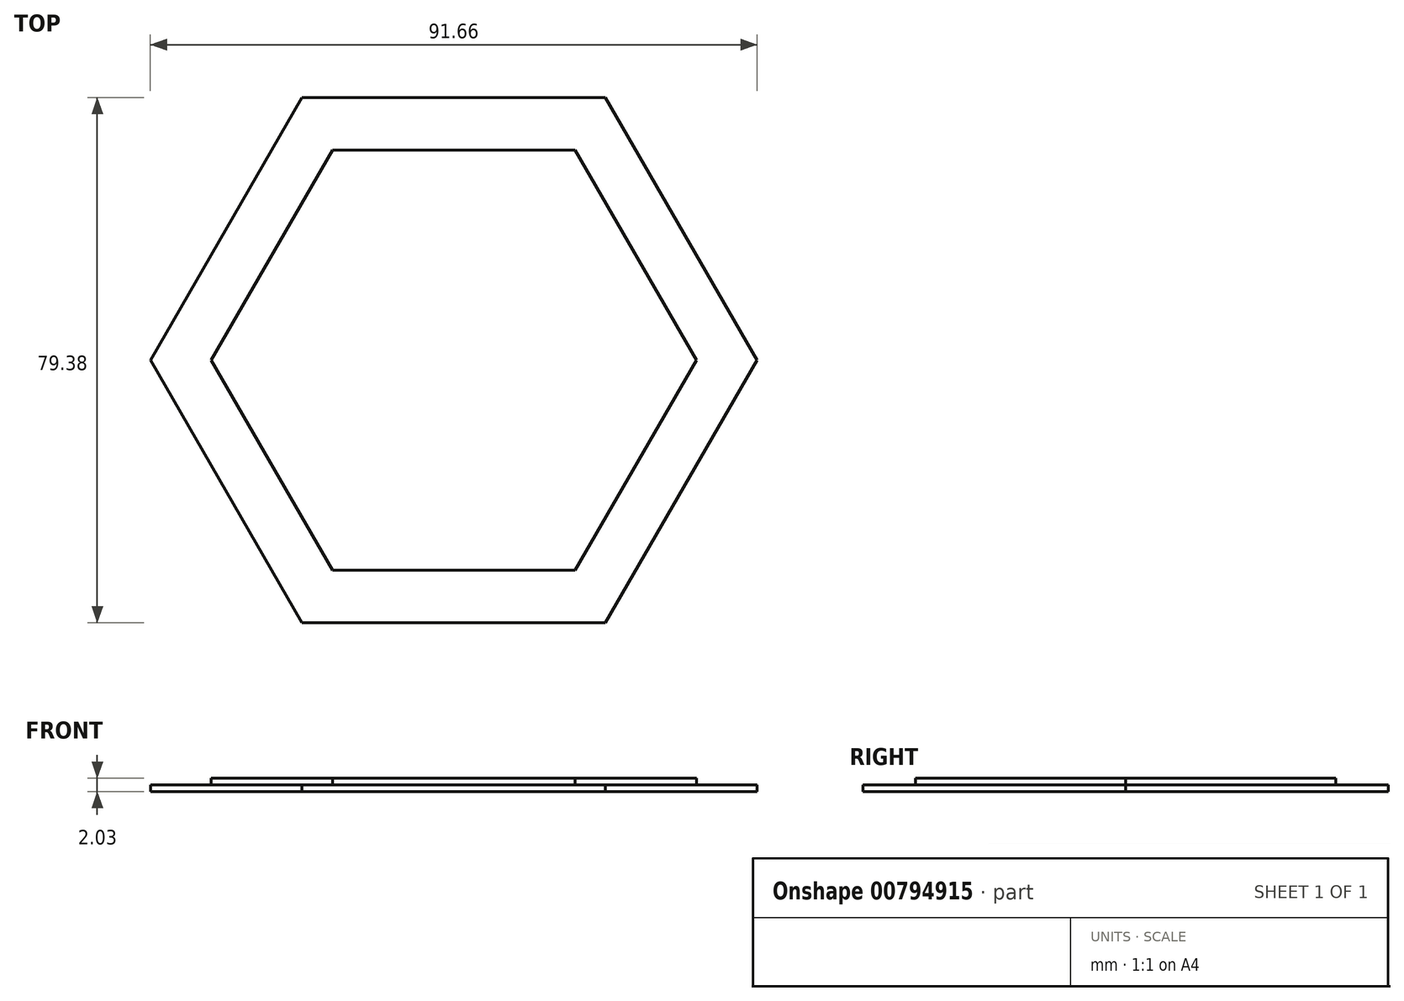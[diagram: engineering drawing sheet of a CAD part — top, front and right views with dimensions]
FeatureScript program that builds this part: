
annotation { "Feature Type Name" : "Feature", "Feature Type Description" : "" }
export const myFeature = defineFeature(function(context is Context, id is Id, definition is map)
    precondition{}
    {
        {
            var Q0;
            Q0=qCreatedBy(makeId("Top.planeOp"),FACE);
            var sketch = newSketch(context, id + "F0", { "sketchPlane" : qUnion([Q0])});
            skCircle(sketch, "E0.cCircle", {"center": v(0, 0) * mm, "radius": 39.69 * mm, "construction": true});
            skLineSegment(sketch, "E0.0", {"start": v(-45.83, 0) * mm, "end": v(-22.91, 39.69) * mm});
            skLineSegment(sketch, "E0.1", {"start": v(-22.91, 39.69) * mm, "end": v(22.91, 39.69) * mm});
            skLineSegment(sketch, "E0.2", {"start": v(22.91, 39.69) * mm, "end": v(45.83, 0) * mm});
            skLineSegment(sketch, "E0.3", {"start": v(45.83, 0) * mm, "end": v(22.91, -39.69) * mm});
            skLineSegment(sketch, "E0.4", {"start": v(22.91, -39.69) * mm, "end": v(-22.91, -39.69) * mm});
            skLineSegment(sketch, "E0.5", {"start": v(-22.91, -39.69) * mm, "end": v(-45.83, 0) * mm});
            skPoint(sketch, "E0.0.midPoint", {"position": v(-34.37, 19.84) * mm});
            skSolve(sketch);
        }
        {
            var Q0;
            Q0=makeQuery(id+"F0.imprint","IMPRINT",FACE,{"disambiguationData":[TD([[makeQuery(id+"F0.imprint","IMPRINT",EDGE,{"derivedFrom":sQuery(id+"F0.wireOp",EDGE,"E0.0")}),-1.0]])]});
            extrude(context, id + "F1", {"entities" : qUnion([Q0]), "depth" : 1.02 * mm, "offsetDistance" : 25.4 * mm});
        }
        {
            var Q0;
            Q0=makeQuery(id+"F1.opExtrude","CAP_FACE",FACE,{"disambiguationData":[OSD([sQuery(id+"F0.wireOp",EDGE,"E0.0"),sQuery(id+"F0.wireOp",EDGE,"E0.1"),sQuery(id+"F0.wireOp",EDGE,"E0.2"),sQuery(id+"F0.wireOp",EDGE,"E0.3"),sQuery(id+"F0.wireOp",EDGE,"E0.4"),sQuery(id+"F0.wireOp",EDGE,"E0.5")])],"isStart":false});
            var sketch = newSketch(context, id + "F2", { "sketchPlane" : qUnion([Q0])});
            skCircle(sketch, "E1.cCircle", {"center": v(0, 0) * mm, "radius": 31.75 * mm, "construction": true});
            skLineSegment(sketch, "E1.0", {"start": v(-36.66, 0) * mm, "end": v(-18.33, 31.75) * mm});
            skLineSegment(sketch, "E1.1", {"start": v(-18.33, 31.75) * mm, "end": v(18.33, 31.75) * mm});
            skLineSegment(sketch, "E1.2", {"start": v(18.33, 31.75) * mm, "end": v(36.66, 0) * mm});
            skLineSegment(sketch, "E1.3", {"start": v(36.66, 0) * mm, "end": v(18.33, -31.75) * mm});
            skLineSegment(sketch, "E1.4", {"start": v(18.33, -31.75) * mm, "end": v(-18.33, -31.75) * mm});
            skLineSegment(sketch, "E1.5", {"start": v(-18.33, -31.75) * mm, "end": v(-36.66, 0) * mm});
            skPoint(sketch, "E1.0.midPoint", {"position": v(-27.5, 15.87) * mm});
            skSolve(sketch);
        }
        {
            var Q0;
            Q0=makeQuery(id+"F2.imprint","IMPRINT",FACE,{"disambiguationData":[TD([[makeQuery(id+"F2.imprint","IMPRINT",EDGE,{"derivedFrom":sQuery(id+"F2.wireOp",EDGE,"E1.0")}),-1.0]])]});
            extrude(context, id + "F3", {"entities" : qUnion([Q0]), "operationType" : NewBodyOperationType.ADD, "depth" : 1.02 * mm, "offsetDistance" : 25.4 * mm});
        }
    });
